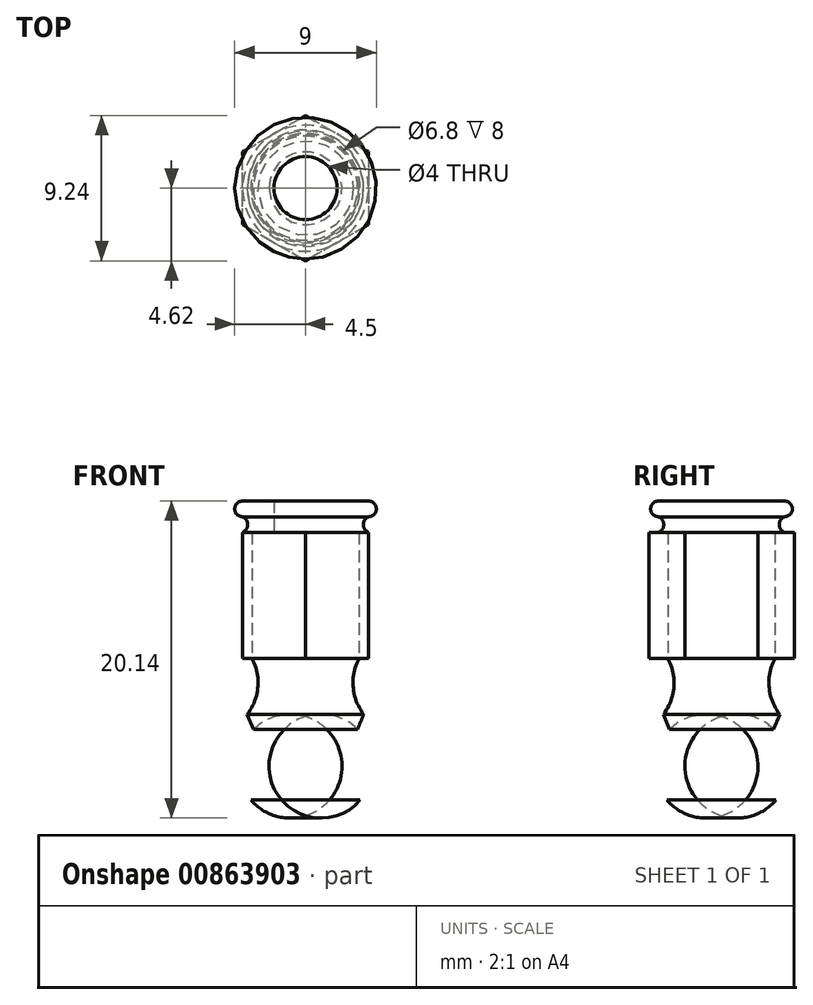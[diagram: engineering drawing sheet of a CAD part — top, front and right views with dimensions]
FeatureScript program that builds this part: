
annotation { "Feature Type Name" : "Feature", "Feature Type Description" : "" }
export const myFeature = defineFeature(function(context is Context, id is Id, definition is map)
    precondition{}
    {
        {
            var Q0;
            Q0=qCreatedBy(makeId("Front.planeOp"),FACE);
            var sketch = newSketch(context, id + "F0", { "sketchPlane" : qUnion([Q0])});
            skLineSegment(sketch, "E0.bottom", {"start": v(-3.4, 0) * mm, "end": v(0, 0) * mm});
            skLineSegment(sketch, "E0.top", {"start": v(-3.47, -9) * mm, "end": v(0, -9) * mm});
            skLineSegment(sketch, "E0.right", {"start": v(0, 0) * mm, "end": v(0, -9) * mm});
            skLineSegment(sketch, "E1", {"start": v(-3.3, -4.5) * mm, "end": v(0, -4.5) * mm, "construction": true});
            skArc(sketch, "E2", {"start": v(-3.3, -4.5) * mm, "mid": v(-4.28, -6.72) * mm, "end": v(-3.47, -9) * mm});
            skArc(sketch, "E3", {"start": v(-3.7, -3.55) * mm, "mid": v(-3.02, -1.82) * mm, "end": v(-3.4, 0) * mm});
            skLineSegment(sketch, "E4", {"start": v(-3.7, -3.55) * mm, "end": v(-3.3, -4.5) * mm});
            skPoint(sketch, "E5.orphan", {"position": v(-4, 0) * mm});
            skPoint(sketch, "E0.left.start.orphan", {"position": v(-4, -4.5) * mm});
            skPoint(sketch, "E6.orphan", {"position": v(-4, -9) * mm});
            skLineSegment(sketch, "E7", {"start": v(0, 5.61) * mm, "end": v(0, -13.18) * mm, "construction": true});
            skSolve(sketch);
        }
        {
            var Q0;
            Q0=makeQuery(id+"F0.imprint","IMPRINT",FACE,{"disambiguationData":[TD([[makeQuery(id+"F0.imprint","IMPRINT",EDGE,{"derivedFrom":sQuery(id+"F0.wireOp",EDGE,"E0.bottom")}),-1.0]])]});
            var Q1;
            Q1=sQuery(id+"F0.wireOp",EDGE,"E7");
            revolve(context, id + "F1", {"surfaceOperationType" : NewSurfaceOperationType.NEW, "entities" : qUnion([Q0]), "axis" : qUnion([Q1]), "revolveType" : RevolveType.FULL});
        }
        {
            var Q0;
            Q0=makeQuery(id+"F1.opRevolve","SWEPT_FACE",FACE,{"disambiguationData":[OSD([sQuery(id+"F0.wireOp",EDGE,"E0.bottom")])]});
            var sketch = newSketch(context, id + "F2", { "sketchPlane" : qUnion([Q0])});
            skCircle(sketch, "E8.cCircle", {"center": v(0, 0) * mm, "radius": 4 * mm, "construction": true});
            skLineSegment(sketch, "E8.0", {"start": v(-4, -2.3) * mm, "end": v(-4, 2.3) * mm});
            skLineSegment(sketch, "E8.1", {"start": v(-4, 2.3) * mm, "end": v(0, 4.62) * mm});
            skLineSegment(sketch, "E8.2", {"start": v(0, 4.62) * mm, "end": v(4, 2.3) * mm});
            skLineSegment(sketch, "E8.3", {"start": v(4, 2.3) * mm, "end": v(4, -2.3) * mm});
            skLineSegment(sketch, "E8.4", {"start": v(4, -2.3) * mm, "end": v(0, -4.62) * mm});
            skLineSegment(sketch, "E8.5", {"start": v(0, -4.62) * mm, "end": v(-4, -2.3) * mm});
            skPoint(sketch, "E8.0.midPoint", {"position": v(-4, 0) * mm});
            skCircle(sketch, "E9", {"center": v(0, 0) * mm, "radius": 1.5 * mm});
            skSolve(sketch);
        }
        {
            var Q0;
            Q0=makeQuery(id+"F2.imprint","IMPRINT",FACE,{"disambiguationData":[TD([[makeQuery(id+"F2.imprint","IMPRINT",EDGE,{"derivedFrom":sQuery(id+"F2.wireOp",EDGE,"E8.0")}),-1.0]])]});
            extrude(context, id + "F3", {"entities" : qUnion([Q0]), "depth" : 8 * mm, "offsetDistance" : 25 * mm});
        }
        {
            var Q0;
            Q0=makeQuery(id+"F3.opExtrude","CAP_FACE",FACE,{"disambiguationData":[OSD([sQuery(id+"F0.wireOp",EDGE,"E0.bottom"),sQuery(id+"F0.wireOp",EDGE,"E3"),sQuery(id+"F2.wireOp",EDGE,"E8.0"),sQuery(id+"F2.wireOp",EDGE,"E8.1"),sQuery(id+"F2.wireOp",EDGE,"E8.2"),sQuery(id+"F2.wireOp",EDGE,"E8.3"),sQuery(id+"F2.wireOp",EDGE,"E8.4"),sQuery(id+"F2.wireOp",EDGE,"E8.5")])],"isStart":false});
            var sketch = newSketch(context, id + "F4", { "sketchPlane" : qUnion([Q0])});
            skCircle(sketch, "E10", {"center": v(0, 0) * mm, "radius": 3.38 * mm});
            skSolve(sketch);
        }
        {
            var Q0;
            Q0=qCreatedBy(makeId("Right.planeOp"),FACE);
            var sketch = newSketch(context, id + "F5", { "sketchPlane" : qUnion([Q0])});
            skLineSegment(sketch, "E11.bottom", {"start": v(0, 8) * mm, "end": v(-4, 8) * mm});
            skLineSegment(sketch, "E11.top", {"start": v(0, 10) * mm, "end": v(-4, 10) * mm});
            skLineSegment(sketch, "E11.left", {"start": v(0, 8) * mm, "end": v(0, 10) * mm});
            skLineSegment(sketch, "E12", {"start": v(-4, 9) * mm, "end": v(0, 9) * mm, "construction": true});
            skArc(sketch, "E13", {"start": v(-4, 10) * mm, "mid": v(-4.5, 9.5) * mm, "end": v(-4, 9) * mm});
            skArc(sketch, "E14", {"start": v(-4, 8) * mm, "mid": v(-3.67, 8.5) * mm, "end": v(-4, 9) * mm});
            skSolve(sketch);
        }
        {
            var Q0;
            Q0=makeQuery(id+"F5.imprint","IMPRINT",FACE,{"disambiguationData":[TD([[makeQuery(id+"F5.imprint","IMPRINT",EDGE,{"derivedFrom":sQuery(id+"F5.wireOp",EDGE,"E11.bottom")}),-1.0]])]});
            var Q1;
            Q1=sQuery(id+"F5.wireOp",EDGE,"E11.left");
            revolve(context, id + "F6", {"surfaceOperationType" : NewSurfaceOperationType.NEW, "entities" : qUnion([Q0]), "axis" : qUnion([Q1]), "revolveType" : RevolveType.FULL});
        }
        {
            var Q0;
            Q0=sQuery(id+"F4.wireOp",VERTEX,"E10.center");
            var Q1;
            Q1=makeQuery(id+"F6.opRevolve","SWEPT_BODY",BODY,{"disambiguationData":[OSD([sQuery(id+"F5.wireOp",EDGE,"E11.bottom"),sQuery(id+"F5.wireOp",EDGE,"E11.top"),sQuery(id+"F5.wireOp",EDGE,"E11.left"),sQuery(id+"F5.wireOp",EDGE,"E13"),sQuery(id+"F5.wireOp",EDGE,"E14")])]});
            hole(context, id + "F7", {"style" : HoleStyle.SIMPLE, "endStyle" : HoleEndStyle.THROUGH, "oppositeDirection" : true, "holeDiameter" : 4 * mm, "majorDiameter" : 5 * mm, "isTappedThrough" : true, "tappedDepth" : 12 * mm, "tapClearance" : 3, "locations" : qUnion([Q0]), "scope" : qUnion([Q1])});
        }
    });
